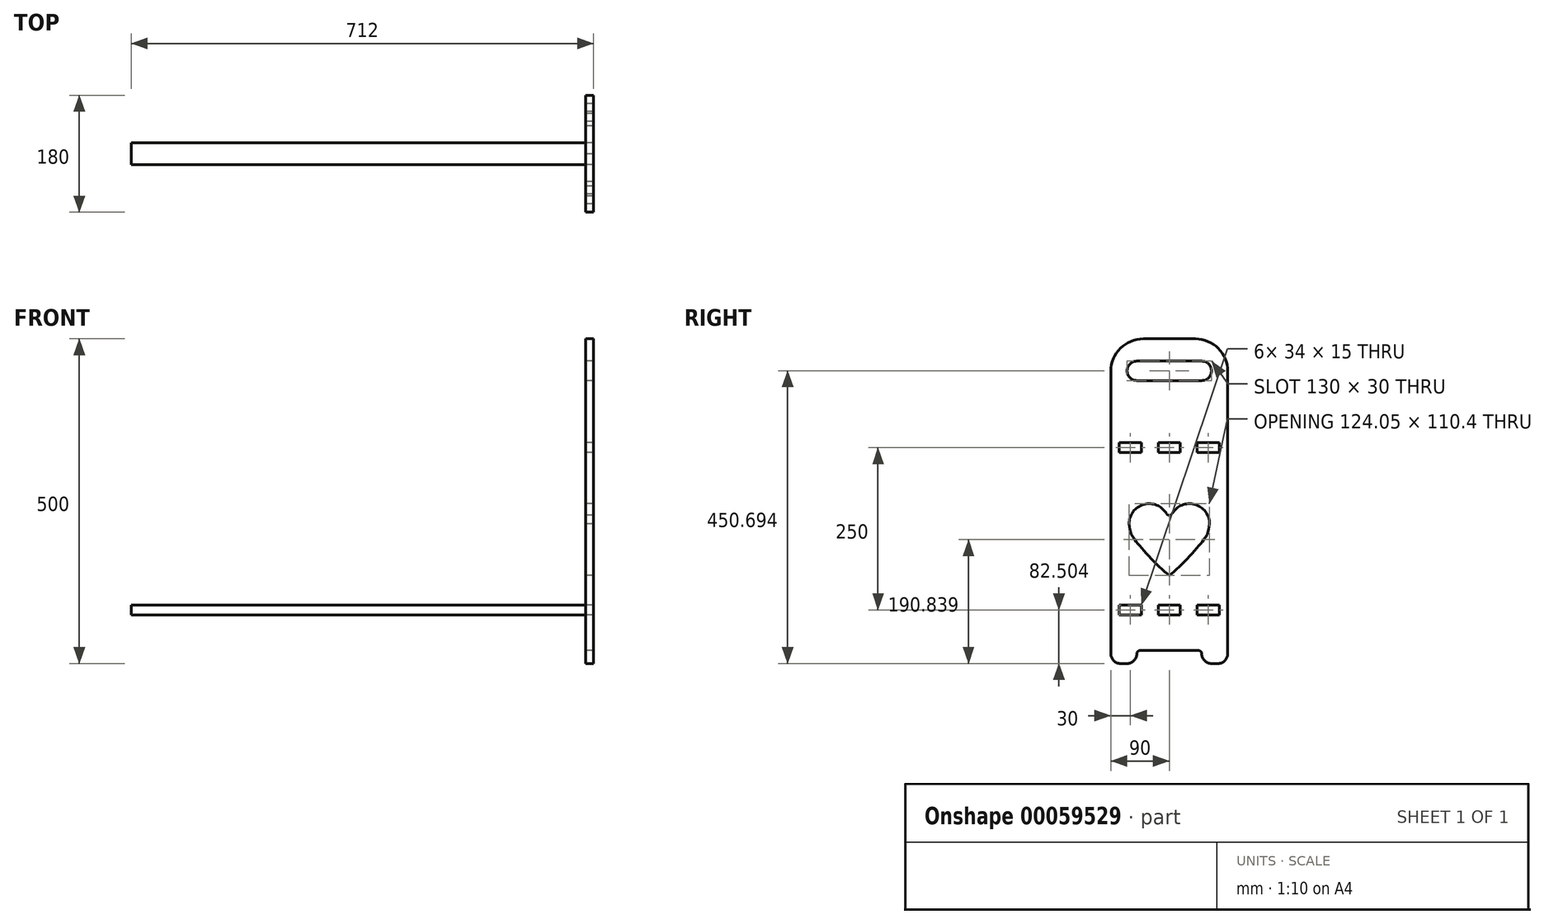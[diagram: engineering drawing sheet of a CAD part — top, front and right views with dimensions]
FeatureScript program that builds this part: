
annotation { "Feature Type Name" : "Feature", "Feature Type Description" : "" }
export const myFeature = defineFeature(function(context is Context, id is Id, definition is map)
    precondition{}
    {
        {
            var Q0;
            Q0=qCreatedBy(makeId("Right.planeOp"),FACE);
            var sketch = newSketch(context, id + "F0", { "sketchPlane" : qUnion([Q0])});
            skLineSegment(sketch, "E0.bottom", {"start": v(-40, 452.1) * mm, "end": v(40, 452.1) * mm});
            skLineSegment(sketch, "E0.top", {"start": v(-75, -47.9) * mm, "end": v(-65, -47.9) * mm});
            skLineSegment(sketch, "E0.left", {"start": v(-90, 402.1) * mm, "end": v(-90, -32.9) * mm});
            skLineSegment(sketch, "E0.right", {"start": v(90, 402.1) * mm, "end": v(90, -32.9) * mm});
            skPoint(sketch, "E1", {"position": v(0, -47.9) * mm});
            skLineSegment(sketch, "E2.bottom", {"start": v(-137, 27.1) * mm, "end": v(-103, 27.1) * mm});
            skLineSegment(sketch, "E2.top", {"start": v(-137, 42.1) * mm, "end": v(-103, 42.1) * mm});
            skLineSegment(sketch, "E2.left", {"start": v(-137, 27.1) * mm, "end": v(-137, 42.1) * mm});
            skLineSegment(sketch, "E2.right", {"start": v(-103, 27.1) * mm, "end": v(-103, 42.1) * mm});
            skLineSegment(sketch, "E3.0.1.0", {"start": v(-103, 277.1) * mm, "end": v(-103, 292.1) * mm});
            skLineSegment(sketch, "E3.0.1.1", {"start": v(-137, 292.1) * mm, "end": v(-103, 292.1) * mm});
            skLineSegment(sketch, "E3.0.1.2", {"start": v(-137, 277.1) * mm, "end": v(-137, 292.1) * mm});
            skLineSegment(sketch, "E3.0.1.3", {"start": v(-137, 277.1) * mm, "end": v(-103, 277.1) * mm});
            skLineSegment(sketch, "E3.1.0.0", {"start": v(-43, 27.1) * mm, "end": v(-43, 42.1) * mm});
            skLineSegment(sketch, "E3.1.0.1", {"start": v(-77, 42.1) * mm, "end": v(-43, 42.1) * mm});
            skLineSegment(sketch, "E3.1.0.2", {"start": v(-77, 27.1) * mm, "end": v(-77, 42.1) * mm});
            skLineSegment(sketch, "E3.1.0.3", {"start": v(-77, 27.1) * mm, "end": v(-43, 27.1) * mm});
            skLineSegment(sketch, "E3.1.1.0", {"start": v(-43, 277.1) * mm, "end": v(-43, 292.1) * mm});
            skLineSegment(sketch, "E3.1.1.1", {"start": v(-77, 292.1) * mm, "end": v(-43, 292.1) * mm});
            skLineSegment(sketch, "E3.1.1.2", {"start": v(-77, 277.1) * mm, "end": v(-77, 292.1) * mm});
            skLineSegment(sketch, "E3.1.1.3", {"start": v(-77, 277.1) * mm, "end": v(-43, 277.1) * mm});
            skLineSegment(sketch, "E3.2.0.0", {"start": v(17, 27.1) * mm, "end": v(17, 42.1) * mm});
            skLineSegment(sketch, "E3.2.0.1", {"start": v(-17, 42.1) * mm, "end": v(17, 42.1) * mm});
            skLineSegment(sketch, "E3.2.0.2", {"start": v(-17, 27.1) * mm, "end": v(-17, 42.1) * mm});
            skLineSegment(sketch, "E3.2.0.3", {"start": v(-17, 27.1) * mm, "end": v(17, 27.1) * mm});
            skLineSegment(sketch, "E3.2.1.0", {"start": v(17, 277.1) * mm, "end": v(17, 292.1) * mm});
            skLineSegment(sketch, "E3.2.1.1", {"start": v(-17, 292.1) * mm, "end": v(17, 292.1) * mm});
            skLineSegment(sketch, "E3.2.1.2", {"start": v(-17, 277.1) * mm, "end": v(-17, 292.1) * mm});
            skLineSegment(sketch, "E3.2.1.3", {"start": v(-17, 277.1) * mm, "end": v(17, 277.1) * mm});
            skLineSegment(sketch, "E3.direction1", {"start": v(-103, 27.1) * mm, "end": v(-43, 27.1) * mm, "construction": true});
            skLineSegment(sketch, "E3.direction2", {"start": v(-103, 27.1) * mm, "end": v(-103, 277.1) * mm, "construction": true});
            skPoint(sketch, "E4", {"position": v(0, 27.1) * mm});
            skLineSegment(sketch, "E5.top", {"start": v(-45, -27.9) * mm, "end": v(45, -27.9) * mm});
            skLineSegment(sketch, "E5.left", {"start": v(-50, -32.9) * mm, "end": v(-50, -32.9) * mm});
            skLineSegment(sketch, "E5.right", {"start": v(50, -32.9) * mm, "end": v(50, -32.9) * mm});
            skLineSegment(sketch, "E6.trimOffspring", {"start": v(65, -47.9) * mm, "end": v(75, -47.9) * mm});
            skPoint(sketch, "E7.visualSharp", {"position": v(-50, -47.9) * mm});
            skArc(sketch, "E7.filletArc", {"start": v(-65, -47.9) * mm, "mid": v(-54.4, -43.51) * mm, "end": v(-50, -32.9) * mm});
            skPoint(sketch, "E8.visualSharp", {"position": v(-90, -47.9) * mm});
            skArc(sketch, "E8.filletArc", {"start": v(-90, -32.9) * mm, "mid": v(-85.6, -43.51) * mm, "end": v(-75, -47.9) * mm});
            skPoint(sketch, "E9.newPointA", {"position": v(50, -22.9) * mm});
            skArc(sketch, "E9.filletArc", {"start": v(50, -32.9) * mm, "mid": v(54.4, -43.51) * mm, "end": v(65, -47.9) * mm});
            skPoint(sketch, "E10.visualSharp", {"position": v(90, -47.9) * mm});
            skArc(sketch, "E10.filletArc", {"start": v(75, -47.9) * mm, "mid": v(85.6, -43.51) * mm, "end": v(90, -32.9) * mm});
            skPoint(sketch, "E11.visualSharp", {"position": v(90, 452.1) * mm});
            skArc(sketch, "E11.filletArc", {"start": v(90, 402.1) * mm, "mid": v(75.36, 437.45) * mm, "end": v(40, 452.1) * mm});
            skPoint(sketch, "E12.visualSharp", {"position": v(-90, 452.1) * mm});
            skArc(sketch, "E12.filletArc", {"start": v(-40, 452.1) * mm, "mid": v(-75.36, 437.45) * mm, "end": v(-90, 402.1) * mm});
            skLineSegment(sketch, "E13.bottom", {"start": v(-50, 417.78) * mm, "end": v(50, 417.78) * mm});
            skLineSegment(sketch, "E13.top", {"start": v(-50, 387.78) * mm, "end": v(50, 387.78) * mm});
            skLineSegment(sketch, "E13.left", {"start": v(-65, 402.78) * mm, "end": v(-65, 402.78) * mm});
            skLineSegment(sketch, "E13.right", {"start": v(65, 402.78) * mm, "end": v(65, 402.78) * mm});
            skLineSegment(sketch, "E14", {"start": v(0, 452.1) * mm, "end": v(0, 417.78) * mm});
            skPoint(sketch, "E15.visualSharp", {"position": v(-65, 417.78) * mm});
            skArc(sketch, "E15.filletArc", {"start": v(-50, 417.78) * mm, "mid": v(-60.6, 413.4) * mm, "end": v(-65, 402.78) * mm});
            skPoint(sketch, "E16.visualSharp", {"position": v(-65, 387.78) * mm});
            skArc(sketch, "E16.filletArc", {"start": v(-65, 402.78) * mm, "mid": v(-60.6, 392.18) * mm, "end": v(-50, 387.78) * mm});
            skPoint(sketch, "E17.visualSharp", {"position": v(65, 417.78) * mm});
            skArc(sketch, "E17.filletArc", {"start": v(65, 402.78) * mm, "mid": v(60.6, 413.4) * mm, "end": v(50, 417.78) * mm});
            skPoint(sketch, "E18.visualSharp", {"position": v(65, 387.78) * mm});
            skArc(sketch, "E18.filletArc", {"start": v(50, 387.78) * mm, "mid": v(60.6, 392.18) * mm, "end": v(65, 402.78) * mm});
            skPoint(sketch, "E19.endSnap0", {"position": v(-60, 277.1) * mm});
            skArc(sketch, "E20", {"start": v(62.03, 167.17) * mm, "mid": v(39.18, 197.09) * mm, "end": v(4.3, 182.93) * mm});
            skFitSpline(sketch, "E21", {"points": [v(0, 87.73) * mm, v(54.1, 144.2) * mm, v(62.03, 167.17) * mm], "startDerivative": vector(92.46, 70.34) * mm, "endDerivative": vector(19.67, 115.1) * mm});
            skFitSpline(sketch, "E22.MirrorCS", {"points": [v(0, 87.73) * mm, v(-54.1, 144.2) * mm, v(-62.03, 167.17) * mm], "startDerivative": vector(-92.46, 70.34) * mm, "endDerivative": vector(-19.67, 115.1) * mm});
            skArc(sketch, "E23.MirrorCS", {"start": v(-62.03, 167.17) * mm, "mid": v(-39.18, 197.09) * mm, "end": v(-4.3, 182.93) * mm});
            skPoint(sketch, "E24.visualSharp", {"position": v(0, 167.17) * mm});
            skArc(sketch, "E24.filletArc", {"start": v(-4.3, 182.93) * mm, "mid": v(0, 180.48) * mm, "end": v(4.3, 182.93) * mm});
            skArc(sketch, "E25.filletArc", {"start": v(-3.14, 90.2) * mm, "mid": v(0, 89.09) * mm, "end": v(3.14, 90.2) * mm});
            skLineSegment(sketch, "E26.0.3.0", {"start": v(77, 27.1) * mm, "end": v(77, 42.1) * mm});
            skLineSegment(sketch, "E26.3.3.0", {"start": v(43, 42.1) * mm, "end": v(77, 42.1) * mm});
            skLineSegment(sketch, "E26.6.3.0", {"start": v(43, 27.1) * mm, "end": v(43, 42.1) * mm});
            skLineSegment(sketch, "E26.9.3.0", {"start": v(43, 27.1) * mm, "end": v(77, 27.1) * mm});
            skLineSegment(sketch, "E26.0.3.1", {"start": v(77, 277.1) * mm, "end": v(77, 292.1) * mm});
            skLineSegment(sketch, "E26.3.3.1", {"start": v(43, 292.1) * mm, "end": v(77, 292.1) * mm});
            skLineSegment(sketch, "E26.6.3.1", {"start": v(43, 277.1) * mm, "end": v(43, 292.1) * mm});
            skLineSegment(sketch, "E26.9.3.1", {"start": v(43, 277.1) * mm, "end": v(77, 277.1) * mm});
            skLineSegment(sketch, "E26.0.4.0", {"start": v(137, 27.1) * mm, "end": v(137, 42.1) * mm});
            skLineSegment(sketch, "E26.3.4.0", {"start": v(103, 42.1) * mm, "end": v(137, 42.1) * mm});
            skLineSegment(sketch, "E26.6.4.0", {"start": v(103, 27.1) * mm, "end": v(103, 42.1) * mm});
            skLineSegment(sketch, "E26.9.4.0", {"start": v(103, 27.1) * mm, "end": v(137, 27.1) * mm});
            skLineSegment(sketch, "E26.0.4.1", {"start": v(137, 277.1) * mm, "end": v(137, 292.1) * mm});
            skLineSegment(sketch, "E26.3.4.1", {"start": v(103, 292.1) * mm, "end": v(137, 292.1) * mm});
            skLineSegment(sketch, "E26.6.4.1", {"start": v(103, 277.1) * mm, "end": v(103, 292.1) * mm});
            skLineSegment(sketch, "E26.9.4.1", {"start": v(103, 277.1) * mm, "end": v(137, 277.1) * mm});
            skPoint(sketch, "E27.visualSharp", {"position": v(-50, -27.9) * mm});
            skArc(sketch, "E27.filletArc", {"start": v(-45, -27.9) * mm, "mid": v(-48.54, -29.37) * mm, "end": v(-50, -32.9) * mm});
            skPoint(sketch, "E28.visualSharp", {"position": v(50, -27.9) * mm});
            skArc(sketch, "E28.filletArc", {"start": v(50, -32.9) * mm, "mid": v(48.54, -29.37) * mm, "end": v(45, -27.9) * mm});
            skSolve(sketch);
        }
        {
            var Q0;
            Q0=makeQuery(id+"F0.imprint","IMPRINT",FACE,{"disambiguationData":[TD([[makeQuery(id+"F0.imprint","IMPRINT",EDGE,{"derivedFrom":sQuery(id+"F0.wireOp",EDGE,"E0.top")}),1.0]])]});
            extrude(context, id + "F1", {"entities" : qUnion([Q0]), "depth" : 12 * mm});
        }
        {
            var Q0;
            Q0=makeQuery(id+"F1.opExtrude","CAP_FACE",FACE,{"disambiguationData":[OSD([sQuery(id+"F0.wireOp",EDGE,"E0.bottom"),sQuery(id+"F0.wireOp",EDGE,"E0.top"),sQuery(id+"F0.wireOp",EDGE,"E0.left"),sQuery(id+"F0.wireOp",EDGE,"E0.right"),sQuery(id+"F0.wireOp",EDGE,"E2.bottom"),sQuery(id+"F0.wireOp",EDGE,"E2.top"),sQuery(id+"F0.wireOp",EDGE,"E2.left"),sQuery(id+"F0.wireOp",EDGE,"E2.right"),sQuery(id+"F0.wireOp",EDGE,"E3.0.1.0"),sQuery(id+"F0.wireOp",EDGE,"E3.0.1.1"),sQuery(id+"F0.wireOp",EDGE,"E3.0.1.2"),sQuery(id+"F0.wireOp",EDGE,"E3.0.1.3"),sQuery(id+"F0.wireOp",EDGE,"E3.1.0.0"),sQuery(id+"F0.wireOp",EDGE,"E3.1.0.1"),sQuery(id+"F0.wireOp",EDGE,"E3.1.0.2"),sQuery(id+"F0.wireOp",EDGE,"E3.1.0.3"),sQuery(id+"F0.wireOp",EDGE,"E3.1.1.0"),sQuery(id+"F0.wireOp",EDGE,"E3.1.1.1"),sQuery(id+"F0.wireOp",EDGE,"E3.1.1.2"),sQuery(id+"F0.wireOp",EDGE,"E3.1.1.3"),sQuery(id+"F0.wireOp",EDGE,"E3.2.0.0"),sQuery(id+"F0.wireOp",EDGE,"E3.2.0.1"),sQuery(id+"F0.wireOp",EDGE,"E3.2.0.2"),sQuery(id+"F0.wireOp",EDGE,"E3.2.0.3"),sQuery(id+"F0.wireOp",EDGE,"E3.2.1.0"),sQuery(id+"F0.wireOp",EDGE,"E3.2.1.1"),sQuery(id+"F0.wireOp",EDGE,"E3.2.1.2"),sQuery(id+"F0.wireOp",EDGE,"E3.2.1.3"),sQuery(id+"F0.wireOp",EDGE,"E5.top"),sQuery(id+"F0.wireOp",EDGE,"E5.left"),sQuery(id+"F0.wireOp",EDGE,"E5.right"),sQuery(id+"F0.wireOp",EDGE,"E6.trimOffspring"),sQuery(id+"F0.wireOp",EDGE,"E7.filletArc"),sQuery(id+"F0.wireOp",EDGE,"E8.filletArc"),sQuery(id+"F0.wireOp",EDGE,"E9.filletArc"),sQuery(id+"F0.wireOp",EDGE,"E10.filletArc"),sQuery(id+"F0.wireOp",EDGE,"E11.filletArc"),sQuery(id+"F0.wireOp",EDGE,"E12.filletArc"),sQuery(id+"F0.wireOp",EDGE,"E13.bottom"),sQuery(id+"F0.wireOp",EDGE,"E13.top"),sQuery(id+"F0.wireOp",EDGE,"E15.filletArc"),sQuery(id+"F0.wireOp",EDGE,"E16.filletArc"),sQuery(id+"F0.wireOp",EDGE,"E17.filletArc"),sQuery(id+"F0.wireOp",EDGE,"E18.filletArc"),sQuery(id+"F0.wireOp",EDGE,"E20"),sQuery(id+"F0.wireOp",EDGE,"E21"),sQuery(id+"F0.wireOp",EDGE,"E22.MirrorCS"),sQuery(id+"F0.wireOp",EDGE,"E23.MirrorCS"),sQuery(id+"F0.wireOp",EDGE,"E24.filletArc"),sQuery(id+"F0.wireOp",EDGE,"E25.filletArc")])],"isStart":true});
            var sketch = newSketch(context, id + "F2", { "sketchPlane" : qUnion([Q0])});
            skLineSegment(sketch, "E29.bottom", {"start": v(-17, 42.1) * mm, "end": v(17, 42.1) * mm});
            skLineSegment(sketch, "E29.top", {"start": v(-17, 27.1) * mm, "end": v(17, 27.1) * mm});
            skLineSegment(sketch, "E29.left", {"start": v(-17, 42.1) * mm, "end": v(-17, 27.1) * mm});
            skLineSegment(sketch, "E29.right", {"start": v(17, 42.1) * mm, "end": v(17, 27.1) * mm});
            skSolve(sketch);
        }
        {
            var Q0;
            Q0=makeQuery(id+"F2.imprint","IMPRINT",FACE,{"disambiguationData":[TD([[makeQuery(id+"F2.imprint","IMPRINT",EDGE,{"derivedFrom":sQuery(id+"F2.wireOp",EDGE,"E29.bottom")}),1.0]])]});
            extrude(context, id + "F3", {"entities" : qUnion([Q0]), "depth" : 700 * mm});
        }
    });
